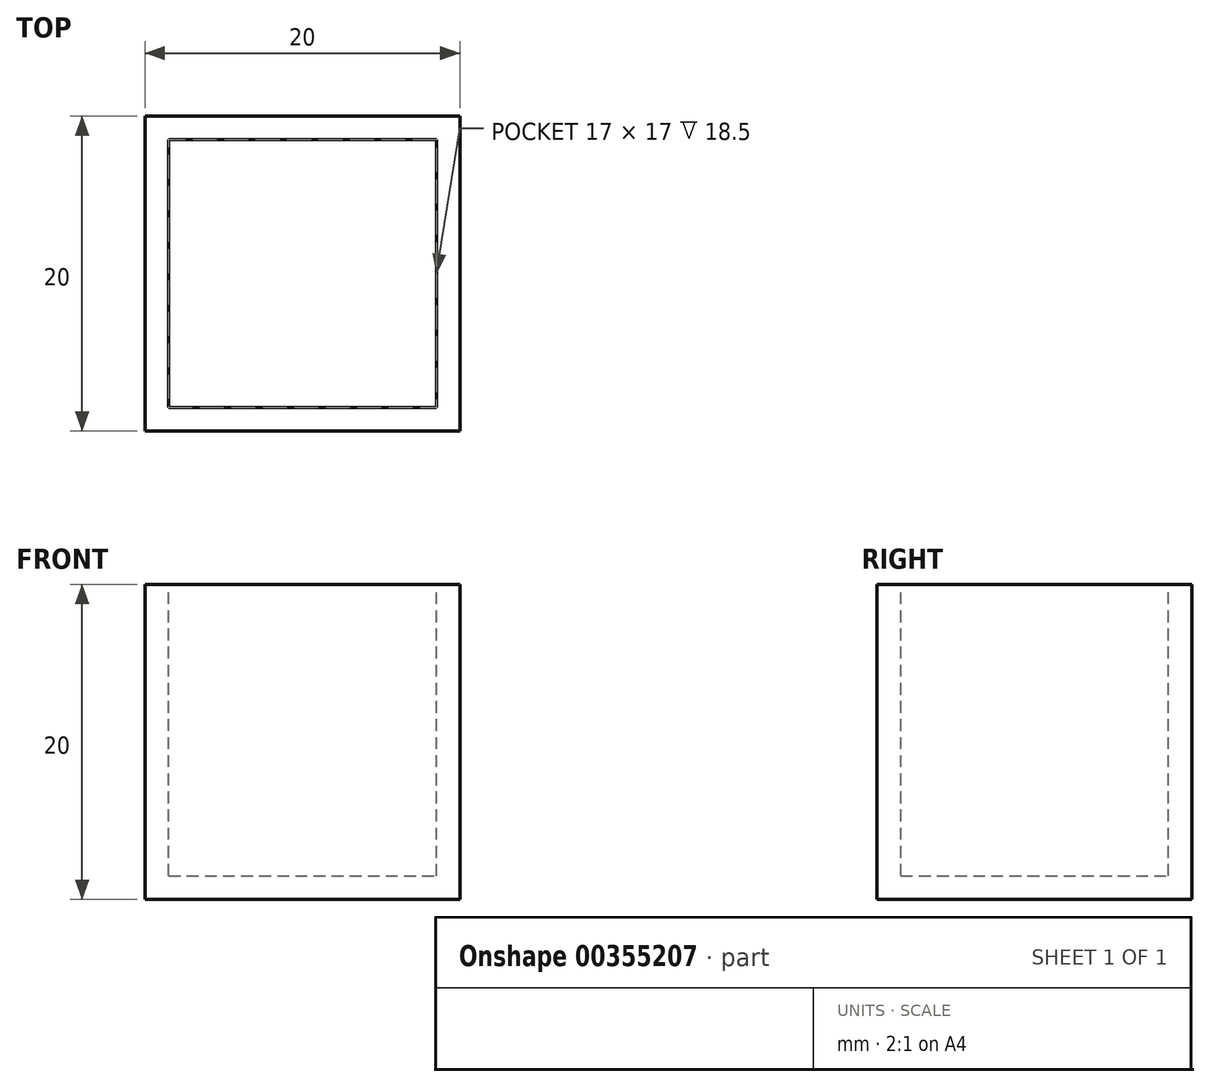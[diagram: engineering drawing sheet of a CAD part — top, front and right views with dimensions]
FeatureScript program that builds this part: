
annotation { "Feature Type Name" : "Feature", "Feature Type Description" : "" }
export const myFeature = defineFeature(function(context is Context, id is Id, definition is map)
    precondition{}
    {
        {
            var Q0;
            Q0=qCreatedBy(makeId("Top.planeOp"),FACE);
            var sketch = newSketch(context, id + "F0", { "sketchPlane" : qUnion([Q0])});
            skLineSegment(sketch, "E0.bottom", {"start": v(10, -10) * mm, "end": v(-10, -10) * mm});
            skLineSegment(sketch, "E0.top", {"start": v(10, 10) * mm, "end": v(-10, 10) * mm});
            skLineSegment(sketch, "E0.left", {"start": v(10, -10) * mm, "end": v(10, 10) * mm});
            skLineSegment(sketch, "E0.right", {"start": v(-10, -10) * mm, "end": v(-10, 10) * mm});
            skPoint(sketch, "E0.middle", {"position": v(0, 0) * mm});
            skSolve(sketch);
        }
        {
            var Q0;
            Q0=makeQuery(id+"F0.imprint","IMPRINT",FACE,{"disambiguationData":[TD([[makeQuery(id+"F0.imprint","IMPRINT",EDGE,{"derivedFrom":sQuery(id+"F0.wireOp",EDGE,"E0.bottom")}),-1.0]])]});
            extrude(context, id + "F1", {"entities" : qUnion([Q0]), "depth" : 20 * mm});
        }
        {
            var Q0;
            Q0=makeQuery(id+"F1.opExtrude","CAP_FACE",FACE,{"disambiguationData":[OSD([sQuery(id+"F0.wireOp",EDGE,"E0.bottom"),sQuery(id+"F0.wireOp",EDGE,"E0.top"),sQuery(id+"F0.wireOp",EDGE,"E0.left"),sQuery(id+"F0.wireOp",EDGE,"E0.right")])],"isStart":false});
            var sketch = newSketch(context, id + "F2", { "sketchPlane" : qUnion([Q0])});
            skLineSegment(sketch, "E1.0", {"start": v(8.5, -8.5) * mm, "end": v(8.5, 8.5) * mm});
            skLineSegment(sketch, "E1.1", {"start": v(-8.5, -8.5) * mm, "end": v(8.5, -8.5) * mm});
            skLineSegment(sketch, "E1.2", {"start": v(-8.5, 8.5) * mm, "end": v(-8.5, -8.5) * mm});
            skLineSegment(sketch, "E1.3", {"start": v(8.5, 8.5) * mm, "end": v(-8.5, 8.5) * mm});
            skSolve(sketch);
        }
        {
            var Q0;
            Q0=makeQuery(id+"F2.imprint","IMPRINT",FACE,{"disambiguationData":[TD([[makeQuery(id+"F2.imprint","IMPRINT",EDGE,{"derivedFrom":sQuery(id+"F2.wireOp",EDGE,"E1.0")}),1.0]])]});
            extrude(context, id + "F3", {"entities" : qUnion([Q0]), "operationType" : NewBodyOperationType.REMOVE, "oppositeDirection" : true, "depth" : (20 - 1.5) * mm});
        }
    });
